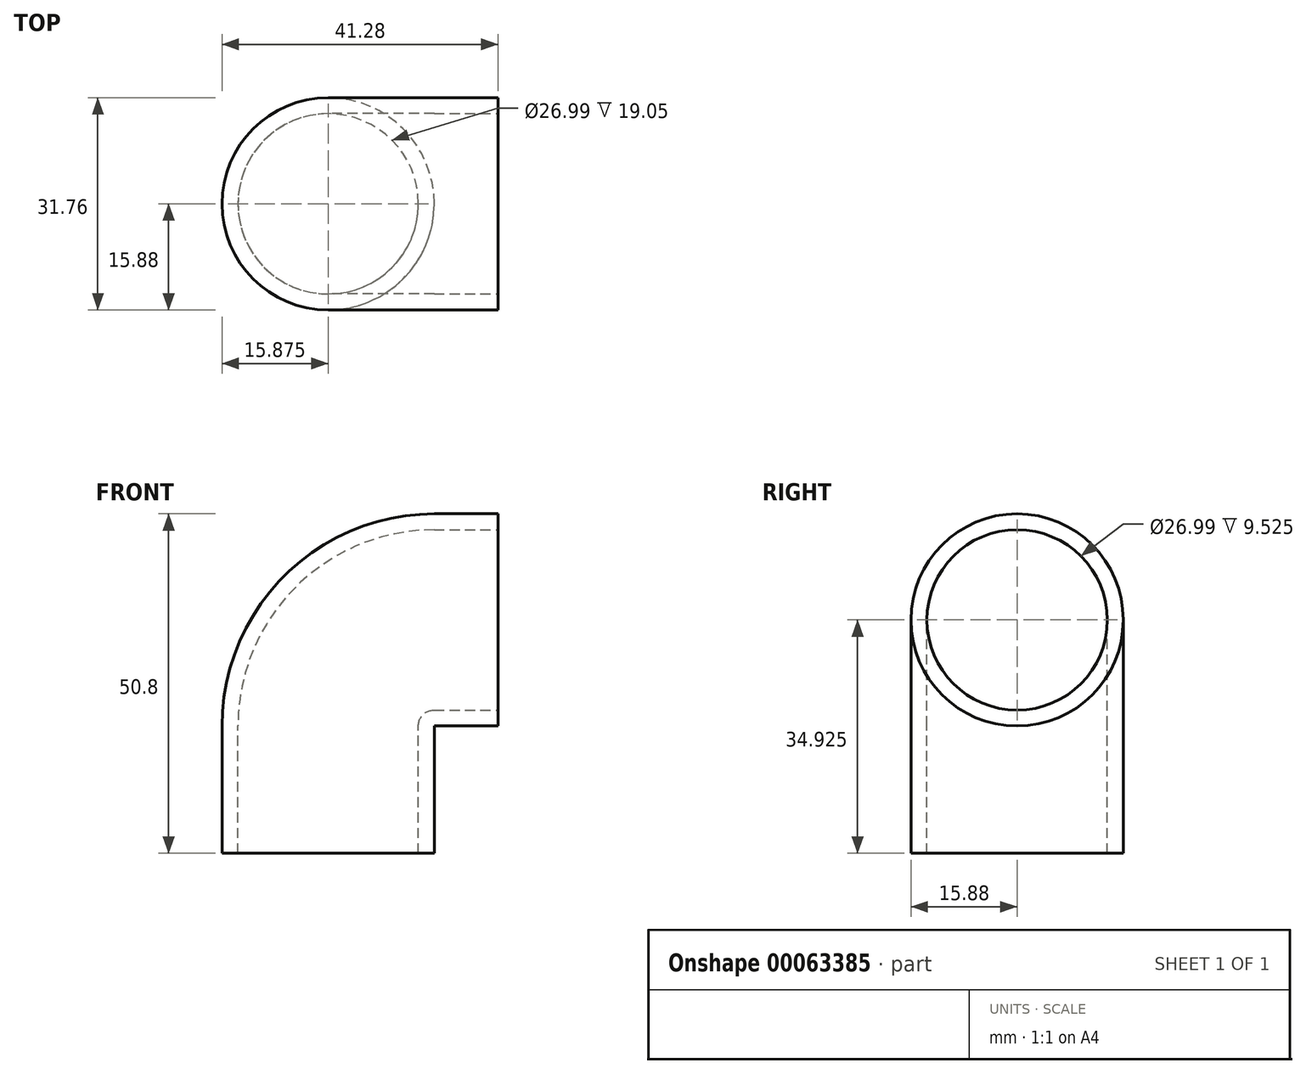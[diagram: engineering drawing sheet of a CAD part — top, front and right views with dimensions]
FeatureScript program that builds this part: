
annotation { "Feature Type Name" : "Feature", "Feature Type Description" : "" }
export const myFeature = defineFeature(function(context is Context, id is Id, definition is map)
    precondition{}
    {
        {
            var Q0;
            Q0=qCreatedBy(makeId("Front.planeOp"),FACE);
            var sketch = newSketch(context, id + "F0", { "sketchPlane" : qUnion([Q0])});
            skLineSegment(sketch, "E0", {"start": v(0, 0) * mm, "end": v(0, 19.05) * mm});
            skLineSegment(sketch, "E1", {"start": v(31.75, 50.8) * mm, "end": v(50.8, 50.8) * mm});
            skPoint(sketch, "E2.visualSharp", {"position": v(0, 50.8) * mm});
            skArc(sketch, "E2.filletArc", {"start": v(31.75, 50.8) * mm, "mid": v(9.3, 41.5) * mm, "end": v(0, 19.05) * mm});
            skSolve(sketch);
        }
        {
            var Q0;
            Q0=qCreatedBy(makeId("Top.planeOp"),FACE);
            var sketch = newSketch(context, id + "F1", { "sketchPlane" : qUnion([Q0])});
            skCircle(sketch, "E3", {"center": v(15.88, 0) * mm, "radius": 15.88 * mm});
            skCircle(sketch, "E4", {"center": v(15.88, 0) * mm, "radius": 13.5 * mm});
            skSolve(sketch);
        }
        {
            var Q0;
            Q0=makeQuery(id+"F1.imprint","IMPRINT",FACE,{"disambiguationData":[TD([[makeQuery(id+"F1.imprint","IMPRINT",EDGE,{"derivedFrom":sQuery(id+"F1.wireOp",EDGE,"E3")}),1.0]])]});
            var Q1;
            Q1=sQuery(id+"F0.wireOp",EDGE,"E0");
            var Q2;
            Q2=sQuery(id+"F0.wireOp",EDGE,"E2.filletArc");
            var Q3;
            Q3=sQuery(id+"F0.wireOp",EDGE,"E1");
            sweep(context, id + "F2", {"profiles" : qUnion([Q0]), "path" : qUnion([Q1, Q2, Q3])});
        }
        {
            var Q0;
            Q0=makeQuery(id+"F2.opSweep","CAP_FACE",FACE,{"disambiguationData":[OSD([sQuery(id+"F0.wireOp",VERTEX,"E1.end"),sQuery(id+"F1.wireOp",EDGE,"E3"),sQuery(id+"F1.wireOp",EDGE,"E4")])],"isStart":false});
            var sketch = newSketch(context, id + "F3", { "sketchPlane" : qUnion([Q0])});
            skCircle(sketch, "E5", {"center": v(0, 34.93) * mm, "radius": 15.95 * mm});
            skSolve(sketch);
        }
        {
            var Q0;
            Q0=qSketchRegion(id+"F3",true);
            extrude(context, id + "F4", {"entities" : qUnion([Q0]), "operationType" : NewBodyOperationType.REMOVE, "oppositeDirection" : true, "depth" : 9.52 * mm});
        }
    });
